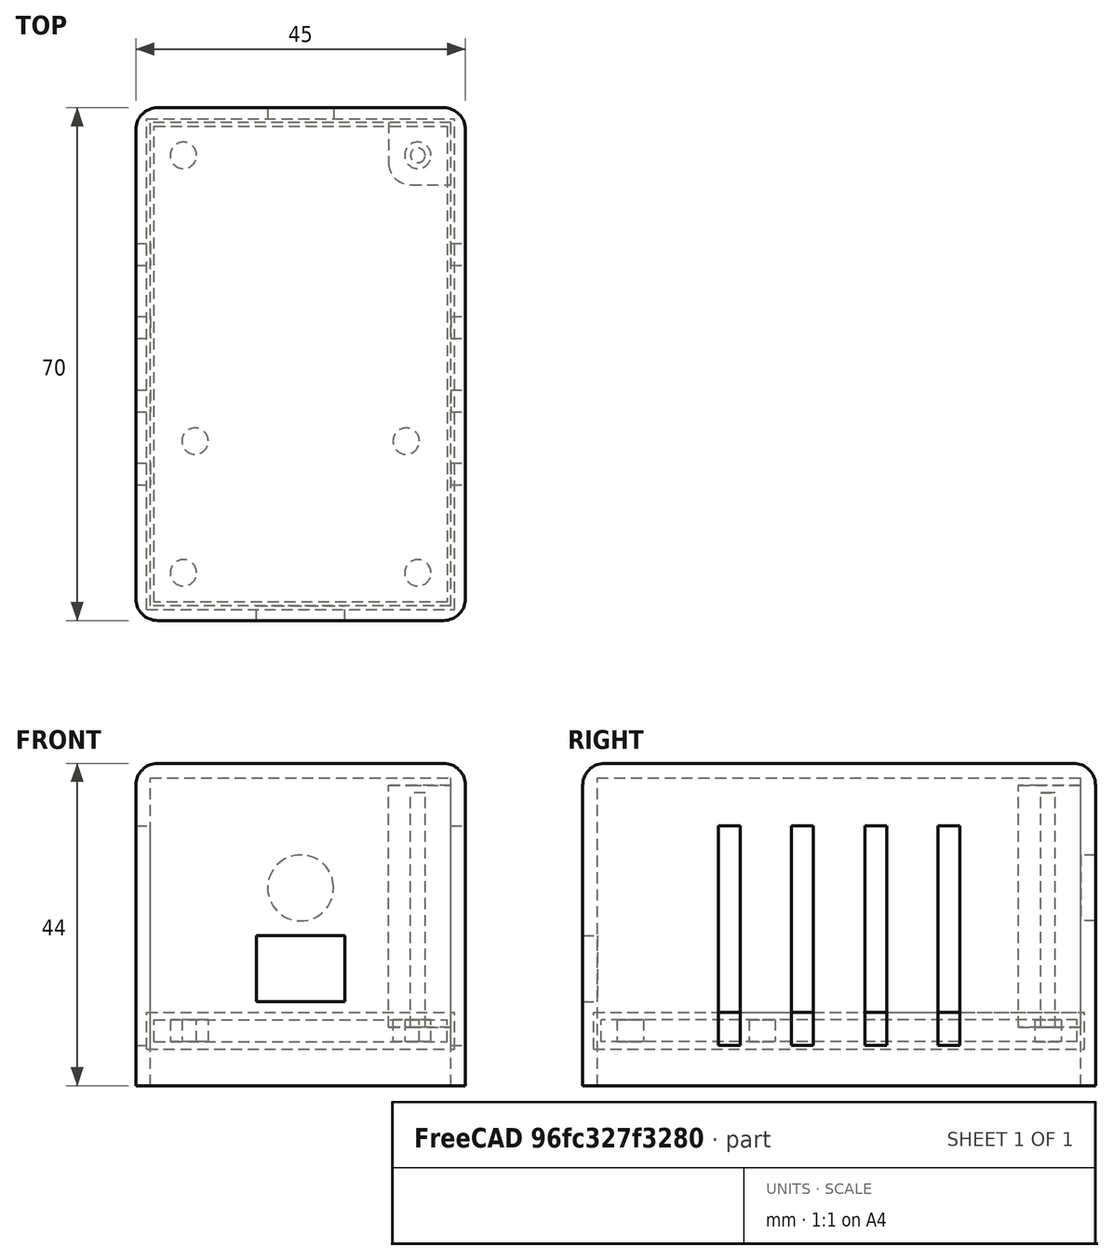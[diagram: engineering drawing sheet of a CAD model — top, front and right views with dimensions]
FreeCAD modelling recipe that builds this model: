
FCSTD DOCUMENT  (FreeCAD 0.18.4R)
Label: ft232rl_box
License: All rights reserved
LicenseURL: http://en.wikipedia.org/wiki/All_rights_reserved
objects: Part::Box×5, Part::FeaturePython×3, Path::FeaturePython×3, Part::Mirroring×3, Part::Cylinder×2, Part::Cut×2, Part::Fillet×2, Part::MultiFuse×2, Mesh::Feature×1, Sketcher::SketchObject×1, PartDesign::Pad×1, PartDesign::Body×1, App::FeaturePython×1, App::DocumentObjectGroup×1, Path::FeatureCompoundPython×1, App::Part×1
note: 23 computed .brp shape members not serialized (recipe doc carries the construction recipe); baked Part::Feature solids carry a one-line shape summary decoded from their .brp

FEATURE [Mesh::Feature] ft232rl
  Placement = pos=(-10.4,0.3,3) rot=(0,0,1;0rad)
FEATURE [Sketcher::SketchObject] Sketch
  MapMode = 5
  Support = -> [XY_Plane]
  sketch-geometry (10):
    g0: LineSegment StartX=-20 StartY=65 StartZ=0 EndX=20 EndY=65 EndZ=0
    g1: LineSegment StartX=20 StartY=65 StartZ=0 EndX=20 EndY=0 EndZ=0
    g2: LineSegment StartX=20 StartY=0 StartZ=0 EndX=-20 EndY=0 EndZ=0
    g3: LineSegment StartX=-20 StartY=0 StartZ=0 EndX=-20 EndY=65 EndZ=0
    g4: Circle CenterX=-14.4 CenterY=22 CenterZ=0 NormalX=0 NormalY=0 NormalZ=1 AngleXU=0 Radius=1.8
    g5: Circle CenterX=14.4 CenterY=22 CenterZ=0 NormalX=0 NormalY=0 NormalZ=1 AngleXU=0 Radius=1.8
    g6: Circle CenterX=-16 CenterY=4 CenterZ=0 NormalX=0 NormalY=0 NormalZ=1 AngleXU=0 Radius=1.8
    g7: Circle CenterX=16 CenterY=4 CenterZ=0 NormalX=0 NormalY=0 NormalZ=1 AngleXU=0 Radius=1.8
    g8: Circle CenterX=16 CenterY=61 CenterZ=0 NormalX=0 NormalY=0 NormalZ=1 AngleXU=0 Radius=1.8
    g9: Circle CenterX=-16 CenterY=61 CenterZ=0 NormalX=0 NormalY=0 NormalZ=1 AngleXU=0 Radius=1.8
  constraints (26):
    c: Coincident(g0,g1)
    c: Coincident(g1,g2)
    c: Coincident(g2,g3)
    c: Coincident(g3,g0)
    c: Horizontal(g0)
    c: Vertical(g1)
    c: Vertical(g3)
    c: Radius(g4) = 1.8
    c: Equal(g5,g4)
    c: DistanceX(g4,g5) = 28.8
    c: DistanceY(g-1,g1) = 0
    c: Symmetric(g1,g2,g-2)
    c: DistanceY(g3,g3) = 65
    c: DistanceX(g0,g0) = 40
    c: DistanceY(g-1,g4) = 22
    c: Symmetric(g4,g5,g-2)
    c: Radius(g6) = 1.8
    c: Equal(g6,g7)
    c: Equal(g7,g8)
    c: Equal(g8,g9)
    c: Symmetric(g6,g7,g-2)
    c: Symmetric(g9,g8,g-2)
    c: DistanceX(g6,g9) = 0
    c: DistanceY(g2,g6) = 4
    c: DistanceX(g2,g6) = 4
    c: DistanceY(g9,g0) = 4
FEATURE [PartDesign::Pad] Pad
  Length = 3
  Length2 = 100
  Profile = -> Sketch
  Type = 0
FEATURE [PartDesign::Body] Body  label="bottom plate body"
  Group = -> [Sketch,Pad]
  Origin = -> Origin
  Tip = -> Pad
FEATURE [App::FeaturePython] SetupSheet  # Path/CAM operation (typed FeaturePython)
  ClearanceHeightExpression = OpStockZMax+SetupSheet.ClearanceHeightOffset
  ClearanceHeightOffset = 0
  FinalDepthExpression = OpFinalDepth
  HorizRapid = 100
  SafeHeightExpression = OpStockZMax+SetupSheet.SafeHeightOffset
  SafeHeightOffset = 0
  StartDepthExpression = OpStartDepth
  StepDownExpression = OpToolDiameter
  VertRapid = 100
FEATURE [Part::FeaturePython] Clone  label="Model-bottom plate body"  # Draft clone (typed FeaturePython)
  AttacherType = Attacher::AttachEngine3D
  Fuse = false
  Objects = -> [Body]
  PathResource = Model
  Scale = (1,1,1)
FEATURE [App::DocumentObjectGroup] Model
  Group = -> [Clone]
FEATURE [Part::FeaturePython] Stock  # WARN: FeaturePython — macro-defined, semantics opaque (R4)
  Base = -> Model
  ExtXneg = 1
  ExtXpos = 1
  ExtYneg = 1
  ExtYpos = 1
  ExtZneg = 1
  ExtZpos = 1
  Placement = pos=(-20,0,0) rot=(0,0,1;0rad)
  StockType = FromBase
FEATURE [Path::FeaturePython] T3__laser  label="T3: laser"  # Path/CAM operation (typed FeaturePython)
  HorizFeed = 0.5
  HorizRapid = 100
  SpindleDir = 0
  SpindleSpeed = 1000
  ToolNumber = 3
  VertFeed = 0.5
  VertRapid = 100
  expr: HorizRapid = SetupSheet.HorizRapid
  expr: VertRapid = SetupSheet.VertRapid
FEATURE [Path::FeaturePython] Engrave  # Path/CAM operation (typed FeaturePython)
  Active = true
  Base = -> [Clone]
  ClearanceHeight = 4
  FinalDepth = 0
  OpFinalDepth = 2.8
  OpStartDepth = 3
  OpStockZMax = 4
  OpStockZMin = -1
  OpToolDiameter = 0.2
  SafeHeight = 4
  StartDepth = 0
  StartVertex = 0
  StepDown = 0.2
  ToolController = -> T3__laser
  expr: ClearanceHeight = OpStockZMax + SetupSheet.ClearanceHeightOffset
  expr: SafeHeight = OpStockZMax + SetupSheet.SafeHeightOffset
  expr: StepDown = OpToolDiameter
FEATURE [Path::FeatureCompoundPython] Operations  # Path/CAM operation (typed FeaturePython)
  Group = -> [Engrave]
  UsePlacements = false
FEATURE [Path::FeaturePython] Job  label="bottom plate job"  # Path/CAM operation (typed FeaturePython)
  GeometryTolerance = 0.01
  Model = -> Model
  Operations = -> Operations
  PostProcessor = 1
  PostProcessorOutputFile = <userpath>/work/roborep/freecad/ft232rl_box/ft232rl_bottom.gcode
  SetupSheet = -> SetupSheet
  Stock = -> Stock
  ToolController = -> [T3__laser]
FEATURE [Part::Box] Box  label="Cube internal"
  AttacherType = Attacher::AttachEngine3D
  Height = 44
  Length = 41
  Placement = pos=(-20.5,-0.5,-8) rot=(0,0,1;0rad)
  Width = 66
FEATURE [Part::Box] Box001  label="Cube outer"
  AttacherType = Attacher::AttachEngine3D
  Height = 44
  Length = 45
  Placement = pos=(-22.5,-2.5,-6) rot=(0,0,1;0rad)
  Width = 70
FEATURE [Part::Box] Box002  label="Cube with hole"
  AttacherType = Attacher::AttachEngine3D
  Height = 33
  Length = 10
  Placement = pos=(0,0,2) rot=(0,0,1;0rad)
  Width = 10
FEATURE [Part::Cylinder] Cylinder
  Angle = 360
  AttacherType = Attacher::AttachEngine3D
  Height = 32
  Placement = pos=(4,6,2) rot=(0,0,1;0rad)
  Radius = 1
FEATURE [Part::Cut] Cut
  Base = -> Box002
  Placement = pos=(12,-2,0) rot=(0,0,1;0rad)
  Tool = -> Cylinder
FEATURE [Part::Fillet] Fillet
  Base = -> Cut
  Edges = 2 edges r=3: [Edge3,Edge6]
FEATURE [Part::Mirroring] Part__Mirroring  label="Cut (Mirror #1)"
  Base = (0,0,0)
  Normal = (1,0,0)
  Source = -> Fillet
FEATURE [Part::Mirroring] Part__Mirroring001  label="Cut (Mirror #2)"
  Base = (0,32.5,0)
  Normal = (0,1,0)
  Source = -> Part__Mirroring
FEATURE [Part::Mirroring] Part__Mirroring002  label="Cut (Mirror #3)"
  Base = (0,0,0)
  Normal = (1,0,0)
  Source = -> Part__Mirroring001
FEATURE [Part::Box] Box003  label="usb hole cube"
  AttacherType = Attacher::AttachEngine3D
  Height = 9
  Length = 12
  Placement = pos=(-6,-8,5.5) rot=(0,0,1;0rad)
  Width = 20
FEATURE [Part::Cylinder] Cylinder001  label="wires hole"
  Angle = 360
  AttacherType = Attacher::AttachEngine3D
  Height = 10
  Placement = pos=(0,73,21) rot=(1,0,0;1.5708rad)
  Radius = 4.5
FEATURE [Part::Box] Box004  label="Cube"
  AttacherType = Attacher::AttachEngine3D
  Height = 30
  Length = 60
  Placement = pos=(-31,16,-0.5) rot=(0,0,1;0rad)
  Width = 3
FEATURE [Part::FeaturePython] Array  # Draft array (typed FeaturePython)
  Angle = 360
  ArrayType = 0
  Axis = (0,0,1)
  Base = -> Box004
  Center = (0,0,0)
  Fuse = false
  IntervalAxis = (0,0,0)
  IntervalX = (1,0,0)
  IntervalY = (0,10,0)
  IntervalZ = (0,0,1)
  NumberPolar = 1
  NumberX = 1
  NumberY = 4
  NumberZ = 1
FEATURE [Part::MultiFuse] Fusion
  Shapes = -> [Box,Box003,Cylinder001,Array]
FEATURE [Part::Cut] Cut001
  Base = -> Box001
  Tool = -> Fusion
FEATURE [Part::MultiFuse] Fusion001
  Shapes = -> [Cut001,Part__Mirroring002]
FEATURE [Part::Fillet] Fillet001
  Base = -> Fusion001
  Edges = 8 edges r=3: [Edge1,Edge2,Edge4,Edge22,Edge23,Edge28,Edge29,Edge36]
FEATURE [App::Part] Part  label="top part"
  Group = -> [Box,Box001,Box002,Cylinder,Cut,Cut001,Part__Mirroring,Part__Mirroring001,Part__Mirroring002,Fillet,Box003,Fusion,Cylinder001,Fusion001,Fillet001,Box004]
  Origin = -> Origin001
